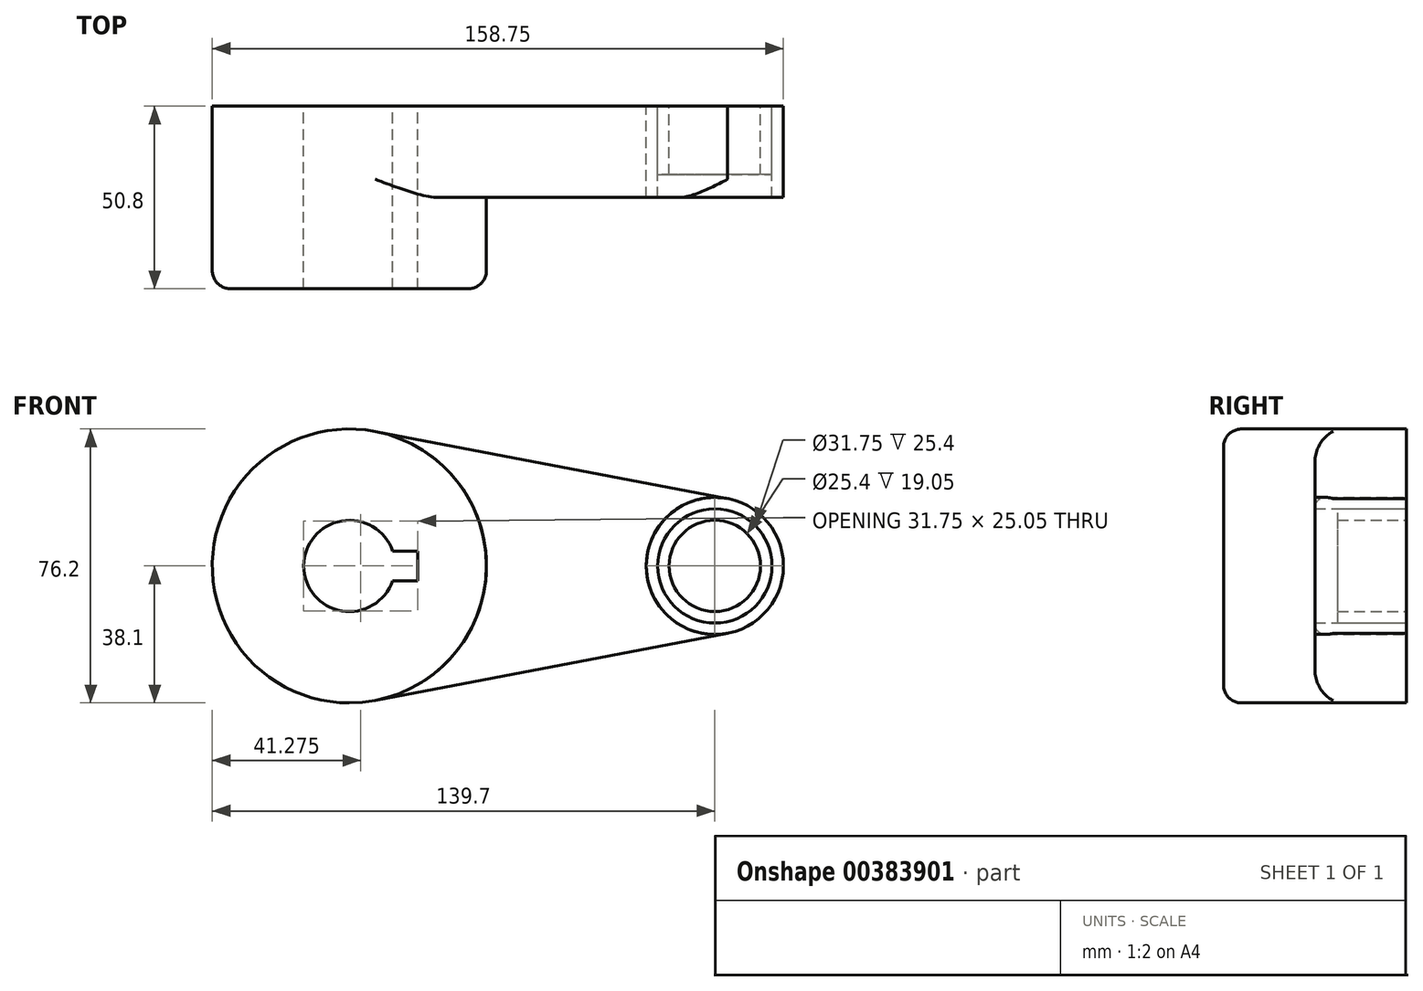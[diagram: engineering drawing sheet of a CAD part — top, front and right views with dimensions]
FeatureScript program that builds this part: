
annotation { "Feature Type Name" : "Feature", "Feature Type Description" : "" }
export const myFeature = defineFeature(function(context is Context, id is Id, definition is map)
    precondition{}
    {
        {
            var Q0;
            Q0=qCreatedBy(makeId("Front.planeOp"),FACE);
            var sketch = newSketch(context, id + "F0", { "sketchPlane" : qUnion([Q0])});
            skCircle(sketch, "E0", {"center": v(0, 0) * mm, "radius": 38.1 * mm});
            skCircle(sketch, "E1", {"center": v(101.6, 0) * mm, "radius": 19.05 * mm});
            skLineSegment(sketch, "E2", {"start": v(7.14, 37.42) * mm, "end": v(105.17, 18.71) * mm});
            skLineSegment(sketch, "E3", {"start": v(7.14, -37.42) * mm, "end": v(105.17, -18.71) * mm});
            skCircle(sketch, "E4", {"center": v(0, 0) * mm, "radius": 12.7 * mm});
            skCircle(sketch, "E5", {"center": v(101.6, 0) * mm, "radius": 12.7 * mm});
            skLineSegment(sketch, "E6.bottom", {"start": v(19.05, -4.13) * mm, "end": v(-19.05, -4.13) * mm});
            skLineSegment(sketch, "E6.top", {"start": v(19.05, 4.13) * mm, "end": v(-19.05, 4.13) * mm});
            skLineSegment(sketch, "E6.left", {"start": v(19.05, -4.13) * mm, "end": v(19.05, 4.13) * mm});
            skLineSegment(sketch, "E6.right", {"start": v(-19.05, -4.13) * mm, "end": v(-19.05, 4.13) * mm});
            skCircle(sketch, "E7", {"center": v(101.6, 0) * mm, "radius": 15.88 * mm});
            skSolve(sketch);
        }
        {
            var Q0;
            {var subQ7=sQuery(id+"F0.wireOp",EDGE,"E6.left");Q0=makeQuery(id+"F0.imprint","IMPRINT",FACE,{"disambiguationData":[TD([[makeQuery(id+"F0.imprint","IMPRINT",EDGE,{"derivedFrom":subQ7}),-1.0]])]});}
            var Q1;
            {var subQ5=sQuery(id+"F0.wireOp",EDGE,"E6.right");Q1=makeQuery(id+"F0.imprint","IMPRINT",FACE,{"disambiguationData":[TD([[makeQuery(id+"F0.imprint","IMPRINT",EDGE,{"derivedFrom":subQ5}),-1.0]])]});}
            var Q2;
            {var subQ0=sQuery(id+"F0.wireOp",EDGE,"E2");Q2=makeQuery(id+"F0.imprint","IMPRINT",FACE,{"disambiguationData":[TD([[makeQuery(id+"F0.imprint","IMPRINT",EDGE,{"derivedFrom":subQ0}),-1.0]])]});}
            var Q3;
            Q3=makeQuery(id+"F0.imprint","IMPRINT",FACE,{"disambiguationData":[TD([[makeQuery(id+"F0.imprint","IMPRINT",EDGE,{"derivedFrom":sQuery(id+"F0.wireOp",EDGE,"E5")}),-1.0]])]});
            extrude(context, id + "F1", {"entities" : qUnion([Q0, Q1, Q2, Q3]), "depth" : 25.4 * mm});
        }
        {
            var Q0;
            {var subQ7=sQuery(id+"F0.wireOp",EDGE,"E6.left");Q0=makeQuery(id+"F0.imprint","IMPRINT",FACE,{"disambiguationData":[TD([[makeQuery(id+"F0.imprint","IMPRINT",EDGE,{"derivedFrom":subQ7}),-1.0]])]});}
            var Q1;
            {var subQ5=sQuery(id+"F0.wireOp",EDGE,"E6.right");Q1=makeQuery(id+"F0.imprint","IMPRINT",FACE,{"disambiguationData":[TD([[makeQuery(id+"F0.imprint","IMPRINT",EDGE,{"derivedFrom":subQ5}),-1.0]])]});}
            extrude(context, id + "F2", {"entities" : qUnion([Q0, Q1]), "operationType" : NewBodyOperationType.ADD, "depth" : 50.8 * mm});
        }
        {
            var Q0;
            Q0=makeQuery(id+"F0.imprint","IMPRINT",FACE,{"disambiguationData":[TD([[makeQuery(id+"F0.imprint","IMPRINT",EDGE,{"derivedFrom":sQuery(id+"F0.wireOp",EDGE,"E7")}),-1.0]])]});
            var Q1;
            Q1=sQuery(id+"F0.wireOp",EDGE,"E1");
            var Q2;
            Q2=sQuery(id+"F0.wireOp",EDGE,"E7");
            extrude(context, id + "F3", {"entities" : qUnion([Q0]), "surfaceEntities" : qUnion([Q1, Q2]), "depth" : 25.4 * mm});
        }
        {
            var Q0;
            Q0=makeQuery(id+"F1.opExtrude","CAP_FACE",FACE,{"disambiguationData":[OSD([sQuery(id+"F0.wireOp",EDGE,"E5"),sQuery(id+"F0.wireOp",EDGE,"E7")])],"isStart":false});
            extrude(context, id + "F4", {"entities" : qUnion([Q0]), "operationType" : NewBodyOperationType.REMOVE, "oppositeDirection" : true, "depth" : 6.35 * mm});
        }
        {
            var Q0;
            Q0=makeQuery(id+"F2.opExtrude","CAP_EDGE",EDGE,{"disambiguationData":[OSD([sQuery(id+"F0.wireOp",EDGE,"E0")])],"isStart":false});
            fillet(context, id + "F5", {"entities" : qUnion([Q0]), "radius" : 5.08 * mm, "tangentPropagation" : true, "allowEdgeOverflow" : false});
        }
        {
            var Q0;
            Q0=makeQuery(id+"F1.opExtrude","CAP_EDGE",EDGE,{"disambiguationData":[OSD([sQuery(id+"F0.wireOp",EDGE,"E2")])],"isStart":false});
            var Q1;
            Q1=makeQuery(id+"F1.opExtrude","CAP_EDGE",EDGE,{"disambiguationData":[OSD([sQuery(id+"F0.wireOp",EDGE,"E3")])],"isStart":false});
            fillet(context, id + "F6", {"entities" : qUnion([Q0, Q1]), "radius" : 5.08 * mm, "tangentPropagation" : true, "allowEdgeOverflow" : false});
        }
    });
